# Revit family: FU_Chair_Sandler_Rose 5-1
name_source: partatom
category: Furniture
units: mm (PartAtom-declared; Revit-internal decimal feet)

## family parameters
Always vertical = Yes
Cut with Voids When Loaded = No
OmniClass Number = 23.40.20.00
OmniClass Title = General Furniture and Specialties
Room Calculation Point = No
Shared = No
Work Plane-Based = No

## types (1)
- Rose 5.1P
    Default Elevation = 0 mm  [stored 0 ft]
    Depth = 600 mm  [stored 1.9685 ft]
    Description = Upholstered lounge chair with ruched detailing on solid wood frame. Metal frames available MOQ 100 and pricing on request.
    Frame = Wood - Beech - 5018 Turquoise Blue
    Height = 750 mm  [stored 2.46063 ft]
    Manufacturer = Sandler
    Model = Rose 5.1P
    Seat = Fabric - Manhattan - Staten YI386
    URL = https://www.sandlerseating.com
    Width = 670 mm  [stored 2.19816 ft]

note: [stored X ft] marks values corroborated as IEEE doubles in the binary element streams (Revit-internal decimal feet)

## geometry (parser evidence)
native form markers: Sweep x3
no freeform markers — native parametric forms only
